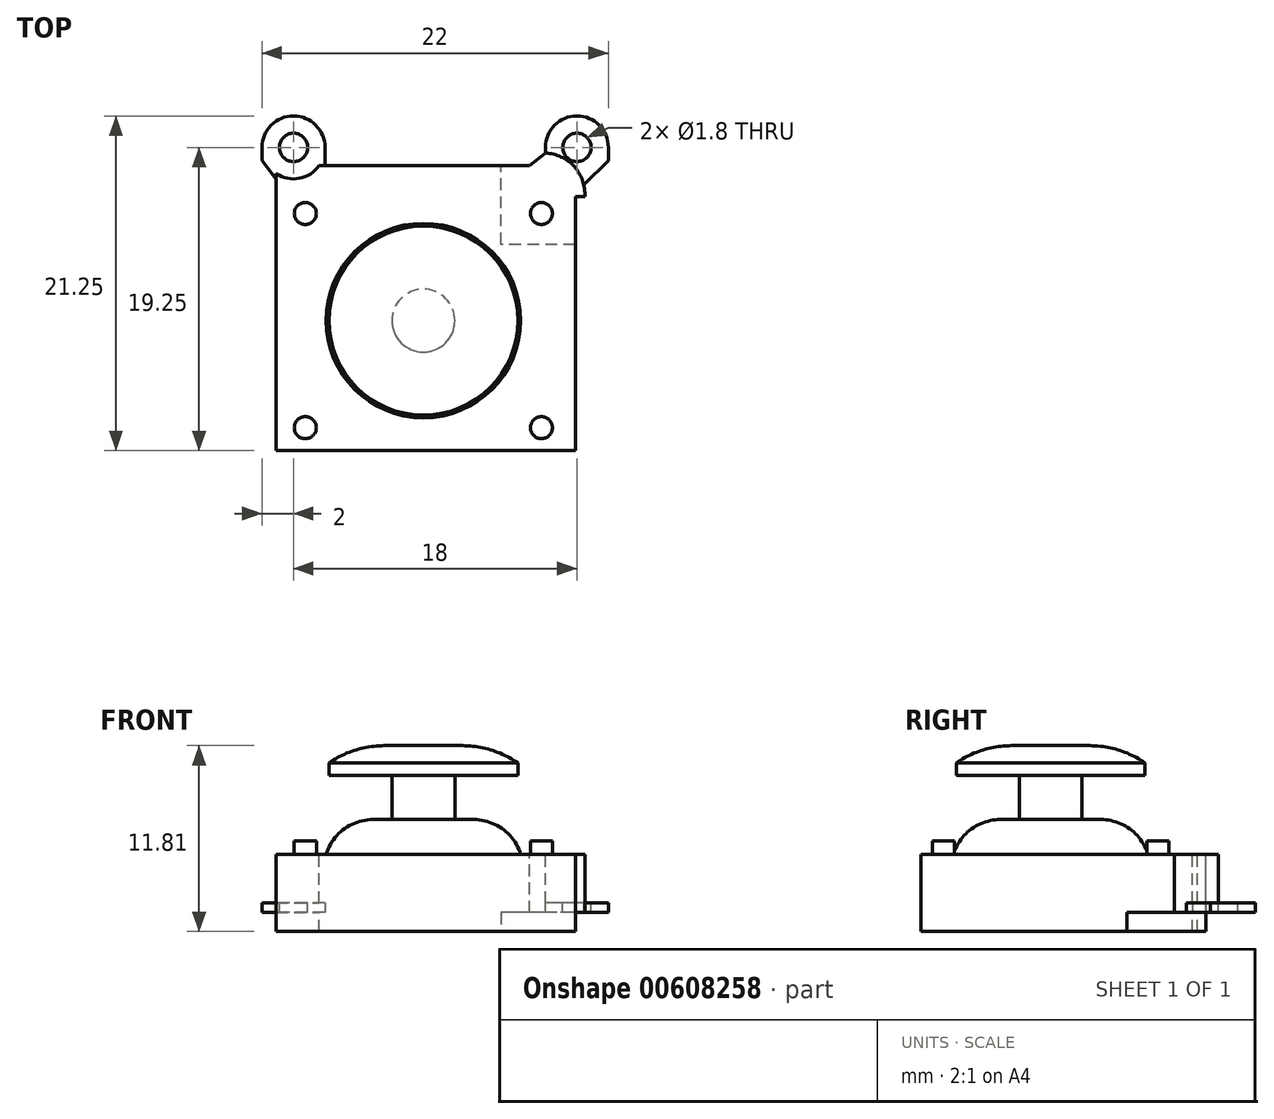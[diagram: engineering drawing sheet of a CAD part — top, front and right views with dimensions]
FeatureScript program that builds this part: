
annotation { "Feature Type Name" : "Feature", "Feature Type Description" : "" }
export const myFeature = defineFeature(function(context is Context, id is Id, definition is map)
    precondition{}
    {
        {
            var Q0;
            Q0=qCreatedBy(makeId("Top.planeOp"),FACE);
            var sketch = newSketch(context, id + "F0", { "sketchPlane" : qUnion([Q0])});
            skLineSegment(sketch, "E0.top", {"start": v(-9.35, -8.25) * mm, "end": v(9.65, -8.25) * mm});
            skLineSegment(sketch, "E0.left", {"start": v(-9.35, 9.33) * mm, "end": v(-9.35, -8.25) * mm});
            skLineSegment(sketch, "E0.right", {"start": v(9.65, 7.87) * mm, "end": v(9.65, -8.25) * mm});
            skArc(sketch, "E1", {"start": v(10.25, 7.87) * mm, "mid": v(9.58, 9.78) * mm, "end": v(7.75, 10.64) * mm});
            skLineSegment(sketch, "E2", {"start": v(-6.61, 9.85) * mm, "end": v(6.75, 9.85) * mm});
            skLineSegment(sketch, "E3", {"start": v(6.75, 9.85) * mm, "end": v(7.75, 10.64) * mm});
            skArc(sketch, "E4", {"start": v(-9.35, 9.33) * mm, "mid": v(-7.88, 9.04) * mm, "end": v(-6.61, 9.85) * mm});
            skLineSegment(sketch, "E5", {"start": v(9.65, 7.87) * mm, "end": v(10.25, 7.87) * mm});
            skSolve(sketch);
        }
        {
            var Q0;
            Q0=qSketchRegion(id+"F0",true);
            extrude(context, id + "F1", {"entities" : qUnion([Q0]), "oppositeDirection" : true, "depth" : 4.9 * mm});
        }
        {
            var Q0;
            Q0=makeQuery(id+"F1.opExtrude","CAP_FACE",FACE,{"disambiguationData":[OSD([sQuery(id+"F0.wireOp",EDGE,"E0.top"),sQuery(id+"F0.wireOp",EDGE,"E0.left"),sQuery(id+"F0.wireOp",EDGE,"E0.right"),sQuery(id+"F0.wireOp",EDGE,"E1"),sQuery(id+"F0.wireOp",EDGE,"E2"),sQuery(id+"F0.wireOp",EDGE,"E3"),sQuery(id+"F0.wireOp",EDGE,"E4"),sQuery(id+"F0.wireOp",EDGE,"E5")])],"isStart":true});
            var sketch = newSketch(context, id + "F2", { "sketchPlane" : qUnion([Q0])});
            skCircle(sketch, "E6", {"center": v(-7.5, -6.8) * mm, "radius": 0.7 * mm});
            skLineSegment(sketch, "E7", {"start": v(0, 5.56) * mm, "end": v(0, -4.06) * mm, "construction": true});
            skLineSegment(sketch, "E8", {"start": v(-3.85, 0) * mm, "end": v(1.78, 0) * mm, "construction": true});
            skCircle(sketch, "E9.0.MirrorC", {"center": v(7.5, -6.8) * mm, "radius": 0.7 * mm});
            skCircle(sketch, "E10.0.MirrorC", {"center": v(-7.5, 6.8) * mm, "radius": 0.7 * mm});
            skCircle(sketch, "E11.0.MirrorC", {"center": v(7.5, 6.8) * mm, "radius": 0.7 * mm});
            skSolve(sketch);
        }
        {
            var Q0;
            Q0=qSketchRegion(id+"F2",true);
            extrude(context, id + "F3", {"entities" : qUnion([Q0]), "operationType" : NewBodyOperationType.ADD, "depth" : 0.85 * mm});
        }
        {
            var Q0;
            Q0=makeQuery(id+"F1.opExtrude","CAP_FACE",FACE,{"disambiguationData":[OSD([sQuery(id+"F0.wireOp",EDGE,"E0.top"),sQuery(id+"F0.wireOp",EDGE,"E0.left"),sQuery(id+"F0.wireOp",EDGE,"E0.right"),sQuery(id+"F0.wireOp",EDGE,"E1"),sQuery(id+"F0.wireOp",EDGE,"E2"),sQuery(id+"F0.wireOp",EDGE,"E3"),sQuery(id+"F0.wireOp",EDGE,"E4"),sQuery(id+"F0.wireOp",EDGE,"E5")])],"isStart":true});
            cPlane(context, id + "F4", {"entities" : qUnion([Q0]), "cplaneType" : CPlaneType.OFFSET, "offset" : 3.1 * mm, "oppositeDirection" : true, "width" : 150 * mm, "height" : 150 * mm});
        }
        {
            var Q0;
            Q0=qCreatedBy(id+"F4.planeOp",FACE);
            var sketch = newSketch(context, id + "F5", { "sketchPlane" : qUnion([Q0])});
            skLineSegment(sketch, "E12", {"start": v(-9.08, 8.65) * mm, "end": v(-10.25, 10.15) * mm});
            skLineSegment(sketch, "E13", {"start": v(-10.25, 10.15) * mm, "end": v(-10.25, 11) * mm});
            skLineSegment(sketch, "E14", {"start": v(-6.25, 11) * mm, "end": v(-6.25, 8.65) * mm});
            skLineSegment(sketch, "E15", {"start": v(-9.08, 8.65) * mm, "end": v(-6.25, 8.65) * mm});
            skLineSegment(sketch, "E16", {"start": v(7.75, 8.43) * mm, "end": v(7.75, 11) * mm});
            skLineSegment(sketch, "E17", {"start": v(11.75, 11) * mm, "end": v(11.75, 10.16) * mm});
            skLineSegment(sketch, "E18", {"start": v(11.75, 10.16) * mm, "end": v(10, 8.43) * mm});
            skLineSegment(sketch, "E19", {"start": v(10, 8.43) * mm, "end": v(7.75, 8.43) * mm});
            skArc(sketch, "E20", {"start": v(-6.25, 11) * mm, "mid": v(-8.25, 13) * mm, "end": v(-10.25, 11) * mm});
            skArc(sketch, "E21", {"start": v(11.75, 11) * mm, "mid": v(9.75, 13) * mm, "end": v(7.75, 11) * mm});
            skSolve(sketch);
        }
        {
            var Q0;
            Q0=qSketchRegion(id+"F5",true);
            extrude(context, id + "F6", {"entities" : qUnion([Q0]), "operationType" : NewBodyOperationType.ADD, "oppositeDirection" : true, "depth" : 0.6 * mm});
        }
        {
            var Q0;
            Q0=makeQuery(id+"F6.opExtrude","CAP_FACE",FACE,{"disambiguationData":[OSD([sQuery(id+"F5.wireOp",EDGE,"E12"),sQuery(id+"F5.wireOp",EDGE,"E13"),sQuery(id+"F5.wireOp",EDGE,"E14"),sQuery(id+"F5.wireOp",EDGE,"E15"),sQuery(id+"F5.wireOp",EDGE,"E20")])],"isStart":true});
            var sketch = newSketch(context, id + "F7", { "sketchPlane" : qUnion([Q0])});
            skCircle(sketch, "E22", {"center": v(-8.25, 11) * mm, "radius": 0.9 * mm});
            skCircle(sketch, "E23.1.0.0", {"center": v(9.75, 11) * mm, "radius": 0.9 * mm});
            skLineSegment(sketch, "E23.direction1", {"start": v(-8.25, 11) * mm, "end": v(9.75, 11) * mm, "construction": true});
            skSolve(sketch);
        }
        {
            var Q0;
            Q0=qSketchRegion(id+"F7",true);
            var Q1;
            Q1=makeQuery(id+"F6.opExtrude","CAP_FACE",FACE,{"disambiguationData":[OSD([sQuery(id+"F5.wireOp",EDGE,"E12"),sQuery(id+"F5.wireOp",EDGE,"E13"),sQuery(id+"F5.wireOp",EDGE,"E14"),sQuery(id+"F5.wireOp",EDGE,"E15"),sQuery(id+"F5.wireOp",EDGE,"E20")])],"isStart":false});
            extrude(context, id + "F8", {"entities" : qUnion([Q0]), "operationType" : NewBodyOperationType.REMOVE, "endBound" : BoundingType.UP_TO_SURFACE, "oppositeDirection" : true, "endBoundEntityFace" : qUnion([Q1]), "depth" : 25 * mm});
        }
        {
            var Q0;
            Q0=qCreatedBy(makeId("Front.planeOp"),FACE);
            var sketch = newSketch(context, id + "F9", { "sketchPlane" : qUnion([Q0])});
            skLineSegment(sketch, "E24", {"start": v(0, 2.2) * mm, "end": v(3.2, 2.2) * mm});
            skLineSegment(sketch, "E25", {"start": v(0, 2.2) * mm, "end": v(0, 0) * mm});
            skLineSegment(sketch, "E26", {"start": v(0, 0) * mm, "end": v(6.18, 0) * mm});
            skArc(sketch, "E27", {"start": v(6.18, 0) * mm, "mid": v(5.05, 1.6) * mm, "end": v(3.2, 2.2) * mm});
            skSolve(sketch);
        }
        {
            var Q0;
            Q0=qSketchRegion(id+"F9",true);
            var Q1;
            Q1=sQuery(id+"F9.wireOp",EDGE,"E25");
            revolve(context, id + "F10", {"operationType" : NewBodyOperationType.ADD, "entities" : qUnion([Q0]), "axis" : qUnion([Q1]), "revolveType" : RevolveType.FULL});
        }
        {
            var Q0;
            Q0=makeQuery(id+"F10.opRevolve","SWEPT_FACE",FACE,{"disambiguationData":[OSD([sQuery(id+"F9.wireOp",EDGE,"E24")])]});
            var sketch = newSketch(context, id + "F11", { "sketchPlane" : qUnion([Q0])});
            skCircle(sketch, "E28", {"center": v(0, 0) * mm, "radius": 2 * mm});
            skSolve(sketch);
        }
        {
            var Q0;
            Q0=qSketchRegion(id+"F11",true);
            extrude(context, id + "F12", {"entities" : qUnion([Q0]), "operationType" : NewBodyOperationType.REMOVE, "oppositeDirection" : true, "depth" : 4 * mm});
        }
        {
            var Q0;
            Q0=qCreatedBy(makeId("Front.planeOp"),FACE);
            var sketch = newSketch(context, id + "F13", { "sketchPlane" : qUnion([Q0])});
            skLineSegment(sketch, "E29", {"start": v(0, -2) * mm, "end": v(0, 6.9) * mm});
            skLineSegment(sketch, "E30", {"start": v(0, 6.9) * mm, "end": v(2.5, 6.9) * mm});
            skLineSegment(sketch, "E31", {"start": v(6, 5.8) * mm, "end": v(6, 5) * mm});
            skLineSegment(sketch, "E32", {"start": v(6, 5) * mm, "end": v(2, 5) * mm});
            skLineSegment(sketch, "E33", {"start": v(2, 5) * mm, "end": v(2, -2) * mm});
            skLineSegment(sketch, "E34", {"start": v(2, -2) * mm, "end": v(0, -2) * mm});
            skArc(sketch, "E35", {"start": v(6, 5.8) * mm, "mid": v(4.33, 6.62) * mm, "end": v(2.5, 6.9) * mm});
            skSolve(sketch);
        }
        {
            var Q0;
            Q0=makeQuery(id+"F13.imprint","IMPRINT",FACE,{"disambiguationData":[TD([[makeQuery(id+"F13.imprint","IMPRINT",EDGE,{"derivedFrom":sQuery(id+"F13.wireOp",EDGE,"E29")}),-1.0]])]});
            var Q1;
            Q1=sQuery(id+"F13.wireOp",EDGE,"E29");
            revolve(context, id + "F14", {"operationType" : NewBodyOperationType.ADD, "entities" : qUnion([Q0]), "axis" : qUnion([Q1]), "revolveType" : RevolveType.FULL});
        }
        {
            var Q0;
            Q0=makeQuery(id+"F1.opExtrude","CAP_FACE",FACE,{"disambiguationData":[OSD([sQuery(id+"F0.wireOp",EDGE,"E0.top"),sQuery(id+"F0.wireOp",EDGE,"E0.left"),sQuery(id+"F0.wireOp",EDGE,"E0.right"),sQuery(id+"F0.wireOp",EDGE,"E1"),sQuery(id+"F0.wireOp",EDGE,"E2"),sQuery(id+"F0.wireOp",EDGE,"E3"),sQuery(id+"F0.wireOp",EDGE,"E4"),sQuery(id+"F0.wireOp",EDGE,"E5")])],"isStart":false});
            var sketch = newSketch(context, id + "F15", { "sketchPlane" : qUnion([Q0])});
            skLineSegment(sketch, "E36.bottom", {"start": v(10.75, -4.84) * mm, "end": v(4.93, -4.84) * mm});
            skLineSegment(sketch, "E36.top", {"start": v(10.75, -10.91) * mm, "end": v(4.93, -10.91) * mm});
            skLineSegment(sketch, "E36.left", {"start": v(10.75, -4.84) * mm, "end": v(10.75, -10.91) * mm});
            skLineSegment(sketch, "E36.right", {"start": v(4.93, -4.84) * mm, "end": v(4.93, -10.91) * mm});
            skSolve(sketch);
        }
        {
            var Q0;
            Q0=qSketchRegion(id+"F15",true);
            var Q1;
            Q1=makeQuery(id+"F6.opExtrude","CAP_FACE",FACE,{"disambiguationData":[OSD([sQuery(id+"F5.wireOp",EDGE,"E16"),sQuery(id+"F5.wireOp",EDGE,"E17"),sQuery(id+"F5.wireOp",EDGE,"E18"),sQuery(id+"F5.wireOp",EDGE,"E19"),sQuery(id+"F5.wireOp",EDGE,"E21")])],"isStart":false});
            extrude(context, id + "F16", {"entities" : qUnion([Q0]), "operationType" : NewBodyOperationType.REMOVE, "endBound" : BoundingType.UP_TO_SURFACE, "oppositeDirection" : true, "endBoundEntityFace" : qUnion([Q1]), "depth" : 25 * mm});
        }
    });
